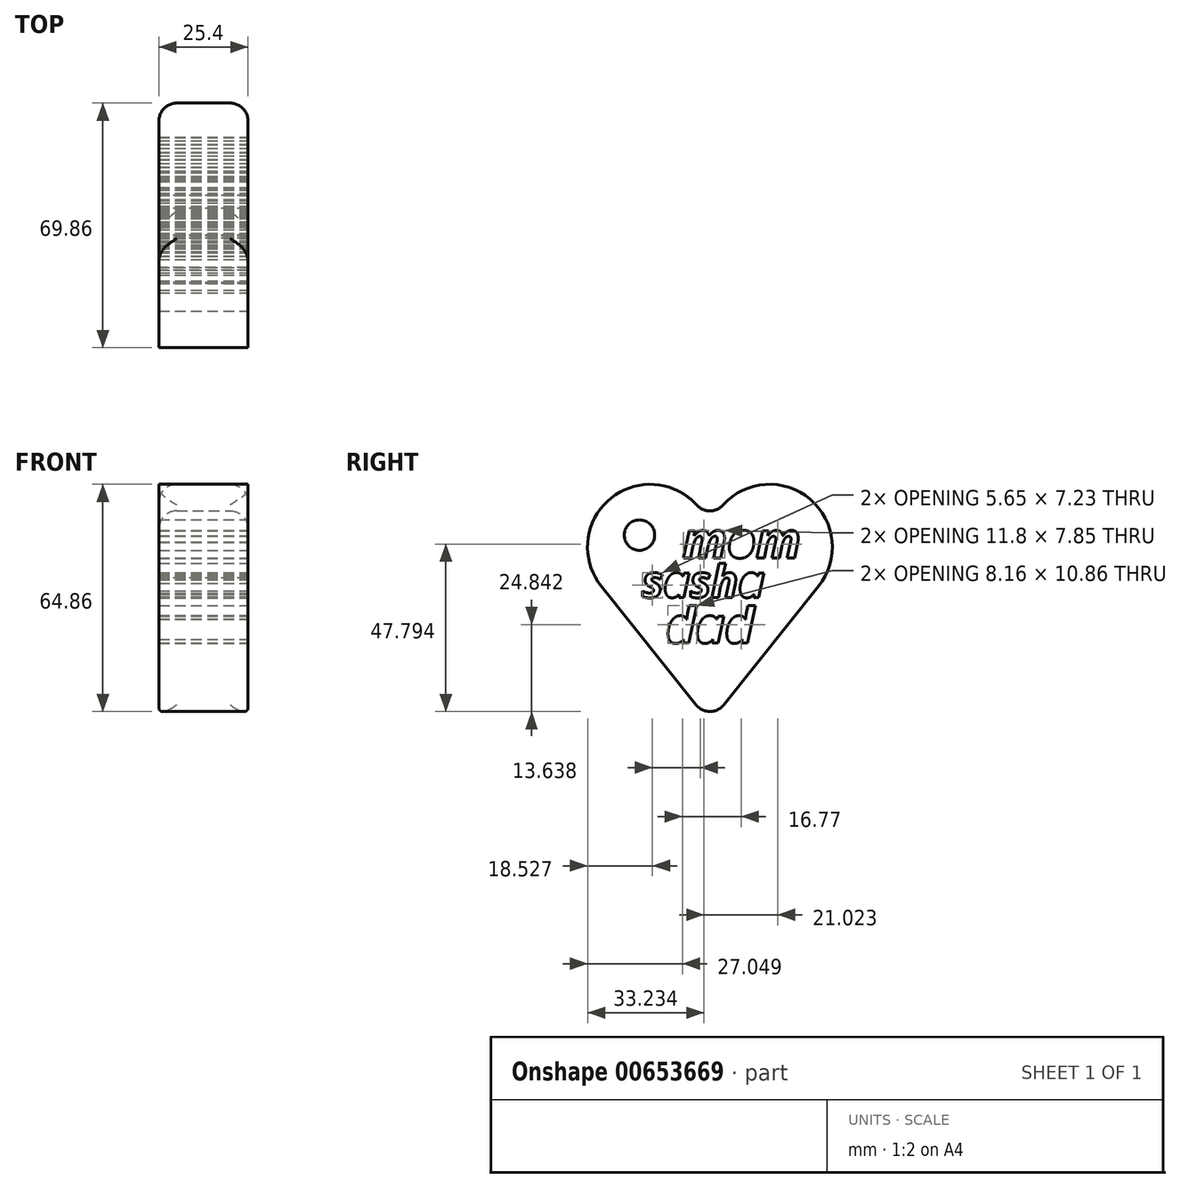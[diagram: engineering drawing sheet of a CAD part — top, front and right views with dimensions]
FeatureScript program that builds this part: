
annotation { "Feature Type Name" : "Feature", "Feature Type Description" : "" }
export const myFeature = defineFeature(function(context is Context, id is Id, definition is map)
    precondition{}
    {
        {
            var Q0;
            Q0=qCreatedBy(makeId("Right.planeOp"),FACE);
            var sketch = newSketch(context, id + "F0", { "sketchPlane" : qUnion([Q0])});
            skLineSegment(sketch, "E0", {"start": v(0, -38.87) * mm, "end": v(31.03, 0) * mm});
            skArc(sketch, "E1", {"start": v(31.03, 0) * mm, "mid": v(25.48, 26.94) * mm, "end": v(0, 16.6) * mm});
            skArc(sketch, "E2.MirrorCS", {"start": v(-31.03, 0) * mm, "mid": v(-25.48, 26.94) * mm, "end": v(0, 16.6) * mm});
            skLineSegment(sketch, "E3.MirrorCS", {"start": v(0, -38.87) * mm, "end": v(-31.03, 0) * mm});
            skSolve(sketch);
        }
        {
            var Q0;
            Q0=qSketchRegion(id+"F0",true);
            extrude(context, id + "F1", {"entities" : qUnion([Q0]), "depth" : 25.4 * mm, "offsetDistance" : 25.4 * mm});
        }
        {
            var Q0;
            Q0=makeQuery(id+"F1.opExtrude","CAP_FACE",FACE,{"disambiguationData":[OSD([sQuery(id+"F0.wireOp",EDGE,"E0"),sQuery(id+"F0.wireOp",EDGE,"E1"),sQuery(id+"F0.wireOp",EDGE,"E2.MirrorCS"),sQuery(id+"F0.wireOp",EDGE,"E3.MirrorCS")])],"isStart":false});
            var sketch = newSketch(context, id + "F2", { "sketchPlane" : qUnion([Q0])});
            skText(sketch, "E4", { "text": "mom\n", "fontName": "OpenSans-BoldItalic.ttf"});
            const initialGuessF2  = {"E4": [-0.00785, 0.00806, 1, 0, 0.01016]};
            skSetInitialGuess(sketch, initialGuessF2);
            skSolve(sketch);
        }
        {
            var Q0;
            Q0=qSketchRegion(id+"F2",true);
            extrude(context, id + "F3", {"entities" : qUnion([Q0]), "operationType" : NewBodyOperationType.REMOVE, "oppositeDirection" : true, "depth" : 152.4 * mm, "offsetDistance" : 25.4 * mm});
        }
        {
            var Q0;
            Q0=makeQuery(id+"F1.opExtrude","SWEPT_FACE",FACE,{"disambiguationData":[OSD([sQuery(id+"F0.wireOp",EDGE,"E1")])]});
            var Q1;
            Q1=makeQuery(id+"F1.opExtrude","SWEPT_EDGE",EDGE,{"disambiguationData":[OSD([sQuery(id+"F0.wireOp",EDGE,"E0"),sQuery(id+"F0.wireOp",EDGE,"E3.MirrorCS")])]});
            fillet(context, id + "F4", {"entities" : qUnion([Q0, Q1]), "radius" : 5.08 * mm, "tangentPropagation" : true, "allowEdgeOverflow" : false});
        }
        {
            var Q0;
            {var subQ0=sQuery(id+"F0.wireOp",EDGE,"E2.MirrorCS");var subQ1=sQuery(id+"F0.wireOp",EDGE,"E0");var subQ2=sQuery(id+"F0.wireOp",EDGE,"E3.MirrorCS");var subQ3=sQuery(id+"F0.wireOp",EDGE,"E1");Q0=makeQuery(id+"F3.boolean.opBoolean","SPLIT",FACE,{"disambiguationData":[TD([makeQuery(id+"F1.opExtrude","SWEPT_FACE",FACE,{"disambiguationData":[OSD([subQ1])]})])],"derivedFrom":makeQuery(id+"F1.opExtrude","CAP_FACE",FACE,{"disambiguationData":[OSD([subQ1,subQ3,subQ0,subQ2])],"isStart":false})});}
            var sketch = newSketch(context, id + "F5", { "sketchPlane" : qUnion([Q0])});
            skCircle(sketch, "E5", {"center": v(-20.12, 14.56) * mm, "radius": 4.35 * mm});
            skSolve(sketch);
        }
        {
            var Q0;
            Q0=makeQuery(id+"F5.imprint","IMPRINT",FACE,{"disambiguationData":[TD([[makeQuery(id+"F5.imprint","IMPRINT",EDGE,{"derivedFrom":sQuery(id+"F5.wireOp",EDGE,"E5")}),1.0]])]});
            extrude(context, id + "F6", {"entities" : qUnion([Q0]), "operationType" : NewBodyOperationType.REMOVE, "oppositeDirection" : true, "depth" : 152.4 * mm, "offsetDistance" : 25.4 * mm});
        }
        {
            var Q0;
            {var subQ0=sQuery(id+"F0.wireOp",EDGE,"E2.MirrorCS");var subQ1=sQuery(id+"F0.wireOp",EDGE,"E0");var subQ2=sQuery(id+"F0.wireOp",EDGE,"E3.MirrorCS");var subQ3=sQuery(id+"F0.wireOp",EDGE,"E1");Q0=makeQuery(id+"F3.boolean.opBoolean","SPLIT",FACE,{"disambiguationData":[TD([makeQuery(id+"F1.opExtrude","SWEPT_FACE",FACE,{"disambiguationData":[OSD([subQ1])]})])],"derivedFrom":makeQuery(id+"F1.opExtrude","CAP_FACE",FACE,{"disambiguationData":[OSD([subQ1,subQ3,subQ0,subQ2])],"isStart":false})});}
            var sketch = newSketch(context, id + "F7", { "sketchPlane" : qUnion([Q0])});
            skText(sketch, "E6", { "text": "dad", "fontName": "OpenSans-BoldItalic.ttf"});
            skText(sketch, "E7", { "text": "sasha", "fontName": "OpenSans-BoldItalic.ttf"});
            const initialGuessF7  = {"E6": [-0.01258, -0.01626, 1, 0, 0.01016], "E7": [-0.01937, -0.00324, 1, 0, 0.0092]};
            skSetInitialGuess(sketch, initialGuessF7);
            skSolve(sketch);
        }
        {
            var Q0;
            Q0 = qSketchRegion(id + "F7", true);
            extrude(context, id + "F8", {"entities" : qUnion([Q0]), "operationType" : NewBodyOperationType.REMOVE, "oppositeDirection" : true, "depth" : 25.4 * mm, "offsetDistance" : 25.4 * mm});
        }
        {
            var Q0;
            Q0=makeQuery(id+"F3.boolean.opBoolean","SPLIT",FACE,{"disambiguationData":[TD([makeQuery(id+"F3.opExtrude","SWEPT_FACE",FACE,{"disambiguationData":[OSD([sQuery(id+"F2.wireOp",EDGE,"E4.sketch_text.stroke-28")])]})])],"derivedFrom":makeQuery(id+"F1.opExtrude","CAP_FACE",FACE,{"disambiguationData":[OSD([sQuery(id+"F0.wireOp",EDGE,"E0"),sQuery(id+"F0.wireOp",EDGE,"E1"),sQuery(id+"F0.wireOp",EDGE,"E2.MirrorCS"),sQuery(id+"F0.wireOp",EDGE,"E3.MirrorCS")])],"isStart":false})});
            extrude(context, id + "F9", {"entities" : qUnion([Q0]), "operationType" : NewBodyOperationType.REMOVE, "oppositeDirection" : true, "depth" : 25.4 * mm, "offsetDistance" : 25.4 * mm});
        }
        {
            var Q0;
            {var subQ0=sQuery(id+"F0.wireOp",EDGE,"E2.MirrorCS");var subQ1=sQuery(id+"F0.wireOp",EDGE,"E0");var subQ2=sQuery(id+"F0.wireOp",EDGE,"E3.MirrorCS");var subQ3=sQuery(id+"F0.wireOp",EDGE,"E1");Q0=makeQuery(id+"F8.boolean.opBoolean","SPLIT",FACE,{"disambiguationData":[TD([makeQuery(id+"F8.opExtrude","SWEPT_FACE",FACE,{"disambiguationData":[OSD([sQuery(id+"F7.wireOp",EDGE,"E7.sketch_text.stroke-38")])]})])],"derivedFrom":makeQuery(id+"F3.boolean.opBoolean","SPLIT",FACE,{"disambiguationData":[TD([makeQuery(id+"F1.opExtrude","SWEPT_FACE",FACE,{"disambiguationData":[OSD([subQ1])]})])],"derivedFrom":makeQuery(id+"F1.opExtrude","CAP_FACE",FACE,{"disambiguationData":[OSD([subQ1,subQ3,subQ0,subQ2])],"isStart":false})})});}
            extrude(context, id + "F10", {"entities" : qUnion([Q0]), "operationType" : NewBodyOperationType.REMOVE, "oppositeDirection" : true, "depth" : 25.4 * mm, "offsetDistance" : 25.4 * mm});
        }
        {
            var Q0;
            {var subQ0=sQuery(id+"F0.wireOp",EDGE,"E2.MirrorCS");var subQ1=sQuery(id+"F0.wireOp",EDGE,"E0");var subQ2=sQuery(id+"F0.wireOp",EDGE,"E3.MirrorCS");var subQ3=sQuery(id+"F0.wireOp",EDGE,"E1");Q0=makeQuery(id+"F8.boolean.opBoolean","SPLIT",FACE,{"disambiguationData":[TD([makeQuery(id+"F8.opExtrude","SWEPT_FACE",FACE,{"disambiguationData":[OSD([sQuery(id+"F7.wireOp",EDGE,"E7.sketch_text.stroke-105")])]})])],"derivedFrom":makeQuery(id+"F3.boolean.opBoolean","SPLIT",FACE,{"disambiguationData":[TD([makeQuery(id+"F1.opExtrude","SWEPT_FACE",FACE,{"disambiguationData":[OSD([subQ1])]})])],"derivedFrom":makeQuery(id+"F1.opExtrude","CAP_FACE",FACE,{"disambiguationData":[OSD([subQ1,subQ3,subQ0,subQ2])],"isStart":false})})});}
            extrude(context, id + "F11", {"entities" : qUnion([Q0]), "operationType" : NewBodyOperationType.REMOVE, "oppositeDirection" : true, "depth" : 25.4 * mm, "offsetDistance" : 25.4 * mm});
        }
        {
            var Q0;
            {var subQ0=sQuery(id+"F0.wireOp",EDGE,"E2.MirrorCS");var subQ1=sQuery(id+"F0.wireOp",EDGE,"E0");var subQ2=sQuery(id+"F0.wireOp",EDGE,"E3.MirrorCS");var subQ3=sQuery(id+"F0.wireOp",EDGE,"E1");Q0=makeQuery(id+"F8.boolean.opBoolean","SPLIT",FACE,{"disambiguationData":[TD([makeQuery(id+"F8.opExtrude","SWEPT_FACE",FACE,{"disambiguationData":[OSD([sQuery(id+"F7.wireOp",EDGE,"E6.sketch_text.stroke-18")])]})])],"derivedFrom":makeQuery(id+"F3.boolean.opBoolean","SPLIT",FACE,{"disambiguationData":[TD([makeQuery(id+"F1.opExtrude","SWEPT_FACE",FACE,{"disambiguationData":[OSD([subQ1])]})])],"derivedFrom":makeQuery(id+"F1.opExtrude","CAP_FACE",FACE,{"disambiguationData":[OSD([subQ1,subQ3,subQ0,subQ2])],"isStart":false})})});}
            extrude(context, id + "F12", {"entities" : qUnion([Q0]), "operationType" : NewBodyOperationType.REMOVE, "oppositeDirection" : true, "depth" : 25.4 * mm, "offsetDistance" : 25.4 * mm});
        }
        {
            var Q0;
            {var subQ0=sQuery(id+"F0.wireOp",EDGE,"E2.MirrorCS");var subQ1=sQuery(id+"F0.wireOp",EDGE,"E0");var subQ2=sQuery(id+"F0.wireOp",EDGE,"E3.MirrorCS");var subQ3=sQuery(id+"F0.wireOp",EDGE,"E1");Q0=makeQuery(id+"F8.boolean.opBoolean","SPLIT",FACE,{"disambiguationData":[TD([makeQuery(id+"F8.opExtrude","SWEPT_FACE",FACE,{"disambiguationData":[OSD([sQuery(id+"F7.wireOp",EDGE,"E6.sketch_text.stroke-42")])]})])],"derivedFrom":makeQuery(id+"F3.boolean.opBoolean","SPLIT",FACE,{"disambiguationData":[TD([makeQuery(id+"F1.opExtrude","SWEPT_FACE",FACE,{"disambiguationData":[OSD([subQ1])]})])],"derivedFrom":makeQuery(id+"F1.opExtrude","CAP_FACE",FACE,{"disambiguationData":[OSD([subQ1,subQ3,subQ0,subQ2])],"isStart":false})})});}
            extrude(context, id + "F13", {"entities" : qUnion([Q0]), "operationType" : NewBodyOperationType.REMOVE, "oppositeDirection" : true, "depth" : 25.4 * mm, "offsetDistance" : 25.4 * mm});
        }
        {
            var Q0;
            {var subQ0=sQuery(id+"F0.wireOp",EDGE,"E2.MirrorCS");var subQ1=sQuery(id+"F0.wireOp",EDGE,"E0");var subQ2=sQuery(id+"F0.wireOp",EDGE,"E3.MirrorCS");var subQ3=sQuery(id+"F0.wireOp",EDGE,"E1");Q0=makeQuery(id+"F8.boolean.opBoolean","SPLIT",FACE,{"disambiguationData":[TD([makeQuery(id+"F8.opExtrude","SWEPT_FACE",FACE,{"disambiguationData":[OSD([sQuery(id+"F7.wireOp",EDGE,"E6.sketch_text.stroke-70")])]})])],"derivedFrom":makeQuery(id+"F3.boolean.opBoolean","SPLIT",FACE,{"disambiguationData":[TD([makeQuery(id+"F1.opExtrude","SWEPT_FACE",FACE,{"disambiguationData":[OSD([subQ1])]})])],"derivedFrom":makeQuery(id+"F1.opExtrude","CAP_FACE",FACE,{"disambiguationData":[OSD([subQ1,subQ3,subQ0,subQ2])],"isStart":false})})});}
            extrude(context, id + "F14", {"entities" : qUnion([Q0]), "operationType" : NewBodyOperationType.REMOVE, "oppositeDirection" : true, "depth" : 25.4 * mm, "offsetDistance" : 25.4 * mm});
        }
    });
